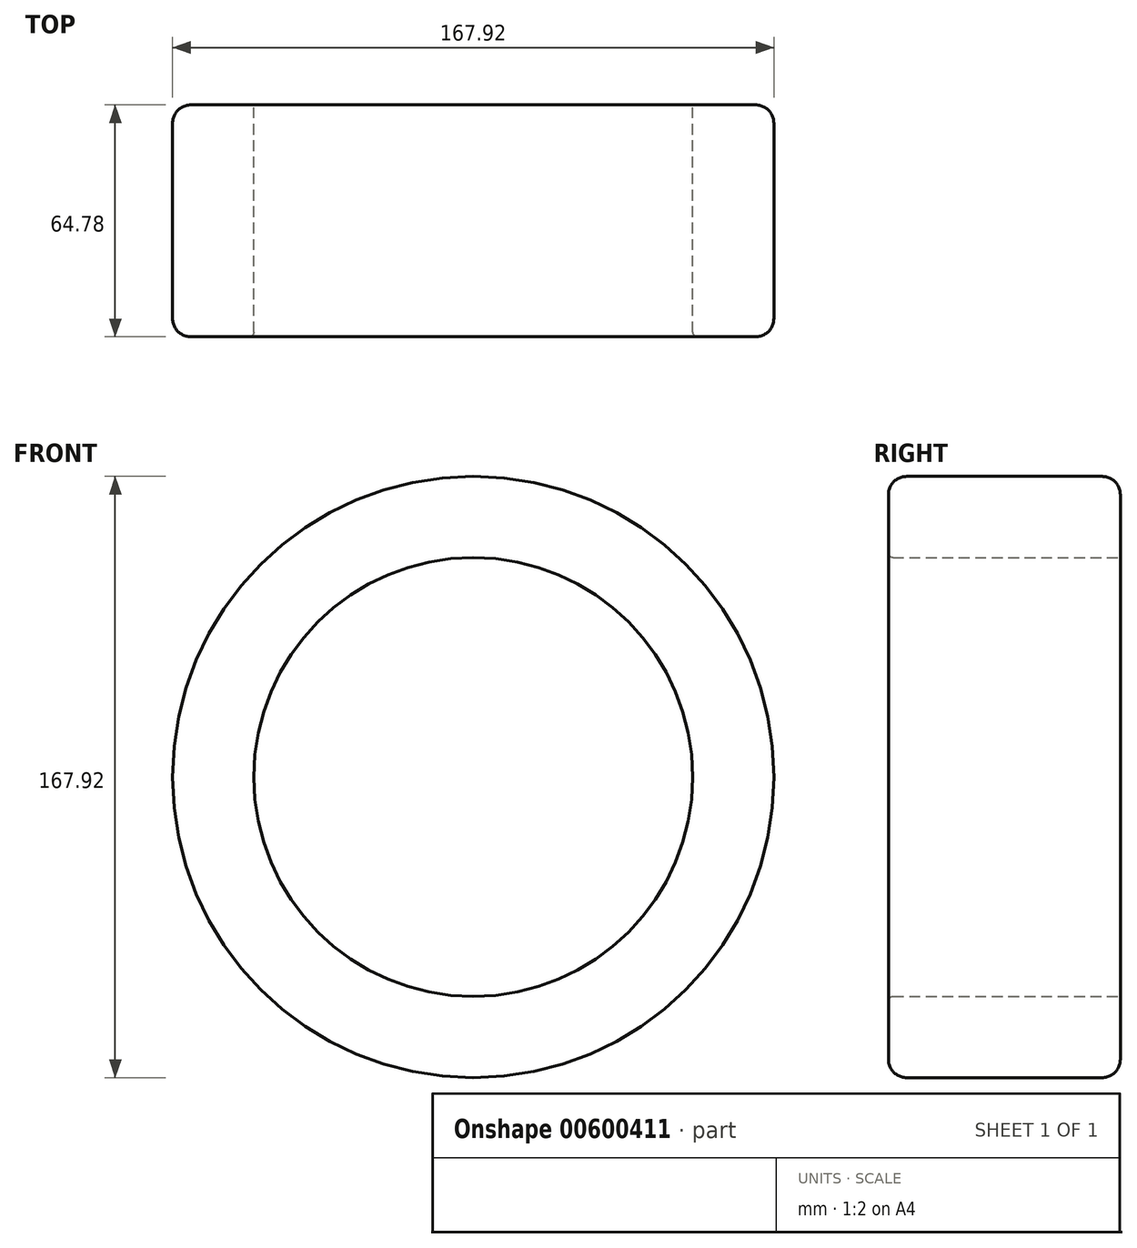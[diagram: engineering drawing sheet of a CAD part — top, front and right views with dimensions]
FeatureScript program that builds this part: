
annotation { "Feature Type Name" : "Feature", "Feature Type Description" : "" }
export const myFeature = defineFeature(function(context is Context, id is Id, definition is map)
    precondition{}
    {
        {
            var Q0;
            Q0=qCreatedBy(makeId("Front.planeOp"),FACE);
            var sketch = newSketch(context, id + "F0", { "sketchPlane" : qUnion([Q0])});
            skCircle(sketch, "E0", {"center": v(0, 0) * mm, "radius": 83.96 * mm});
            skSolve(sketch);
        }
        {
            var Q0;
            Q0=makeQuery(id+"F0.imprint","IMPRINT",FACE,{"disambiguationData":[TD([[makeQuery(id+"F0.imprint","IMPRINT",EDGE,{"derivedFrom":sQuery(id+"F0.wireOp",EDGE,"E0")}),1.0]])]});
            extrude(context, id + "F1", {"entities" : qUnion([Q0]), "endBound" : BoundingType.SYMMETRIC, "depth" : 64.77 * mm, "offsetDistance" : 25.4 * mm});
        }
        {
            var Q0;
            Q0=qCreatedBy(makeId("Front.planeOp"),FACE);
            var sketch = newSketch(context, id + "F2", { "sketchPlane" : qUnion([Q0])});
            skCircle(sketch, "E1", {"center": v(0, 0) * mm, "radius": 61.3 * mm});
            skSolve(sketch);
        }
        {
            var Q0;
            Q0 = qSketchRegion(id + "F2", true);
            extrude(context, id + "F3", {"entities" : qUnion([Q0]), "operationType" : NewBodyOperationType.REMOVE, "endBound" : BoundingType.SYMMETRIC, "depth" : 101.6 * mm, "offsetDistance" : 25.4 * mm});
        }
        {
            var Q0;
            Q0=makeQuery(id+"F1.opExtrude","CAP_EDGE",EDGE,{"disambiguationData":[OSD([sQuery(id+"F0.wireOp",EDGE,"E0")])],"isStart":false});
            var Q1;
            Q1=makeQuery(id+"F1.opExtrude","CAP_EDGE",EDGE,{"disambiguationData":[OSD([sQuery(id+"F0.wireOp",EDGE,"E0")])],"isStart":true});
            fillet(context, id + "F4", {"entities" : qUnion([Q0, Q1]), "radius" : 5.08 * mm, "tangentPropagation" : true, "allowEdgeOverflow" : false});
        }
        {
            var Q0;
            Q0=makeQuery(id+"F3.boolean.opBoolean","INTERSECT",EDGE,{"derivedFrom":[makeQuery(id+"F1.opExtrude","CAP_FACE",FACE,{"disambiguationData":[OSD([sQuery(id+"F0.wireOp",EDGE,"E0")])],"isStart":false}),makeQuery(id+"F3.opExtrude","SWEPT_FACE",FACE,{"disambiguationData":[OSD([sQuery(id+"F2.wireOp",EDGE,"E1")])]})]});
            var Q1;
            Q1=makeQuery(id+"F3.boolean.opBoolean","COPY",EDGE,{"derivedFrom":makeQuery(id+"F3.opExtrude","CAP_EDGE",EDGE,{"disambiguationData":[OSD([sQuery(id+"F2.wireOp",EDGE,"E1")])],"isStart":true})});
            fillet(context, id + "F5", {"entities" : qUnion([Q0, Q1]), "radius" : 1.27 * mm, "tangentPropagation" : true, "allowEdgeOverflow" : false});
        }
    });
